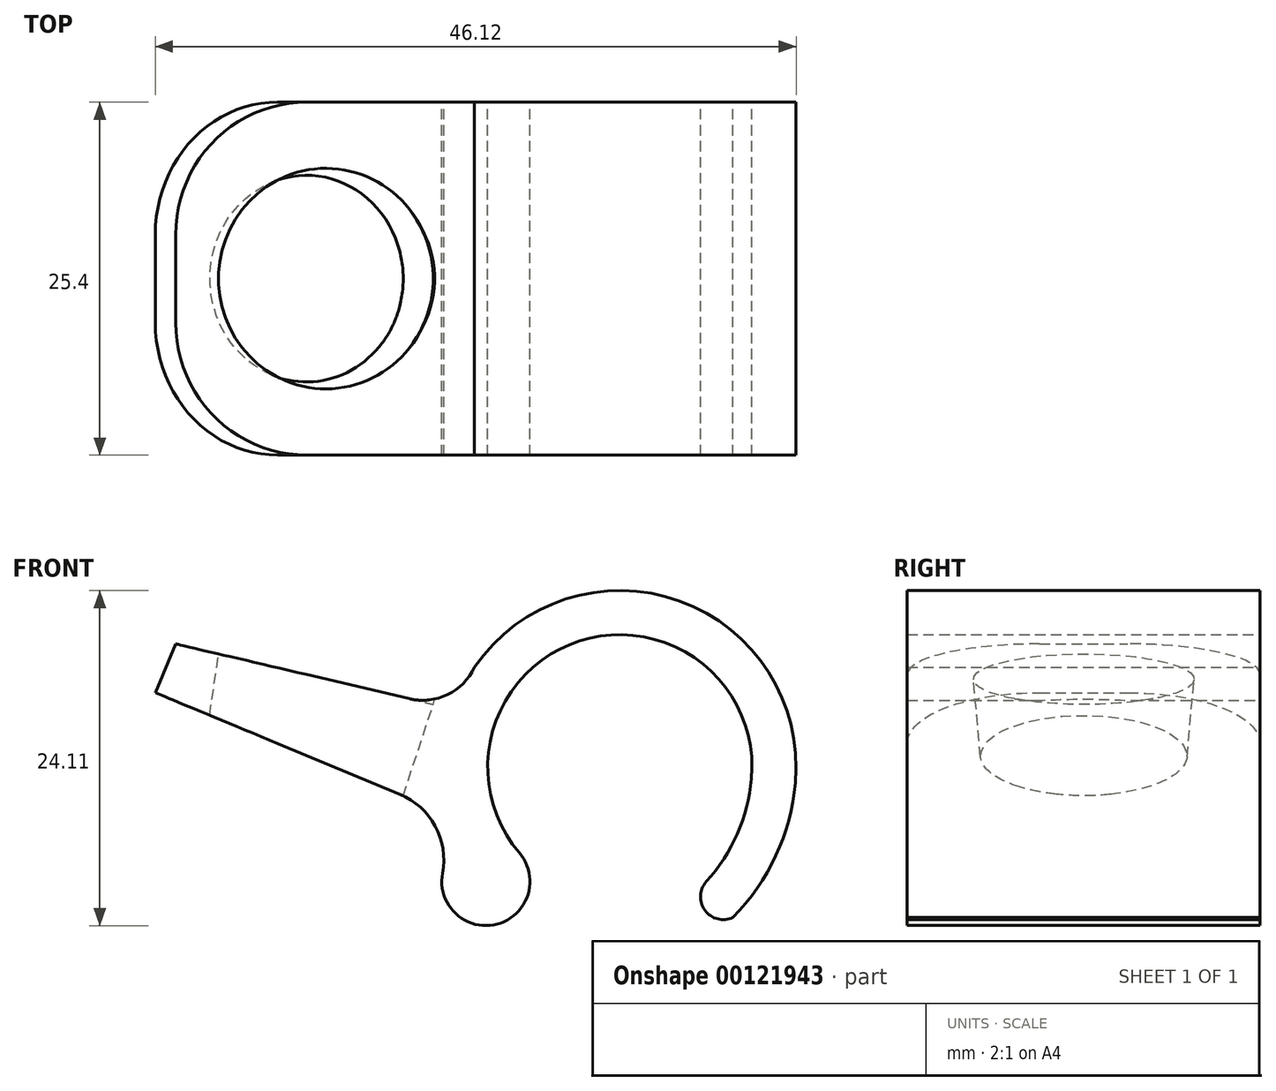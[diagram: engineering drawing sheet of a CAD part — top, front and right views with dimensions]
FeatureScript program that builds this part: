
annotation { "Feature Type Name" : "Feature", "Feature Type Description" : "" }
export const myFeature = defineFeature(function(context is Context, id is Id, definition is map)
    precondition{}
    {
        {
            var Q0;
            Q0=qCreatedBy(makeId("Front.planeOp"),FACE);
            var sketch = newSketch(context, id + "F0", { "sketchPlane" : qUnion([Q0])});
            skLineSegment(sketch, "E0.bottom", {"start": v(0, 0) * mm, "end": v(12.7, 0) * mm, "construction": true});
            skLineSegment(sketch, "E0.top", {"start": v(0, -39.58) * mm, "end": v(12.7, -39.58) * mm, "construction": true});
            skLineSegment(sketch, "E0.left", {"start": v(0, 0) * mm, "end": v(0, -39.58) * mm, "construction": true});
            skLineSegment(sketch, "E0.right", {"start": v(12.7, 0) * mm, "end": v(12.7, -39.58) * mm, "construction": true});
            skArc(sketch, "E1", {"start": v(12.7, -12.7) * mm, "mid": v(14.92, -9.28) * mm, "end": v(15.94, -5.33) * mm});
            skArc(sketch, "E2", {"start": v(-6.3, -12.11) * mm, "mid": v(-2.36, -15.77) * mm, "end": v(-0.76, -10.64) * mm});
            skArc(sketch, "E3", {"start": v(15.94, -5.33) * mm, "mid": v(3.59, 4.6) * mm, "end": v(-0.76, -10.64) * mm});
            skArc(sketch, "E4", {"start": v(-6.3, -12.11) * mm, "mid": v(-6.82, -8.72) * mm, "end": v(-9.37, -6.42) * mm});
            skLineSegment(sketch, "E5", {"start": v(-9.37, -6.42) * mm, "end": v(-26.96, 0.88) * mm});
            skArc(sketch, "E6.0", {"start": v(19.1, -5.62) * mm, "mid": v(10.77, 7.48) * mm, "end": v(-4, 2.72) * mm});
            skArc(sketch, "E6.1", {"start": v(14.62, -15.3) * mm, "mid": v(17.7, -10.84) * mm, "end": v(19.1, -5.62) * mm});
            skArc(sketch, "E7", {"start": v(-8.68, 0.45) * mm, "mid": v(-5.93, 0.75) * mm, "end": v(-4, 2.72) * mm});
            skLineSegment(sketch, "E8", {"start": v(-26.96, 0.88) * mm, "end": v(-25.5, 4.4) * mm});
            skLineSegment(sketch, "E9", {"start": v(-25.5, 4.4) * mm, "end": v(-8.68, 0.45) * mm});
            skArc(sketch, "E10", {"start": v(12.7, -12.7) * mm, "mid": v(12.6, -14.78) * mm, "end": v(14.62, -15.3) * mm});
            skLineSegment(sketch, "E11", {"start": v(12.7, -12.7) * mm, "end": v(14.62, -15.3) * mm, "construction": true});
            skSolve(sketch);
        }
        {
            var Q0;
            Q0 = qSketchRegion(id + "F0", true);
            extrude(context, id + "F1", {"entities" : qUnion([Q0]), "depth" : 25.4 * mm});
        }
        {
            var Q0;
            Q0=makeQuery(id+"F1.opExtrude","SWEPT_FACE",FACE,{"disambiguationData":[OSD([sQuery(id+"F0.wireOp",EDGE,"E9")])]});
            var sketch = newSketch(context, id + "F2", { "sketchPlane" : qUnion([Q0])});
            skCircle(sketch, "E12", {"center": v(-14.72, -12.7) * mm, "radius": 7.94 * mm});
            skLineSegment(sketch, "E13", {"start": v(-25.83, -12.7) * mm, "end": v(-14.72, -12.7) * mm, "construction": true});
            skPoint(sketch, "E14", {"position": v(-22.66, -12.7) * mm});
            skSolve(sketch);
        }
        {
            var Q0;
            Q0 = qSketchRegion(id + "F2", true);
            extrude(context, id + "F3", {"entities" : qUnion([Q0]), "operationType" : NewBodyOperationType.REMOVE, "oppositeDirection" : true, "depth" : 25.4 * mm, "hasDraft" : true, "draftAngle" : 5 * degree, "draftPullDirection" : true, "hasSecondDirection" : true, "secondDirectionOppositeDirection" : false, "secondDirectionDepth" : 25.4 * mm});
        }
        {
            var Q0;
            Q0=makeQuery(id+"F1.opExtrude","CAP_EDGE",EDGE,{"disambiguationData":[OSD([sQuery(id+"F0.wireOp",EDGE,"E8")])],"isStart":true});
            var Q1;
            Q1=makeQuery(id+"F1.opExtrude","CAP_EDGE",EDGE,{"disambiguationData":[OSD([sQuery(id+"F0.wireOp",EDGE,"E8")])],"isStart":false});
            fillet(context, id + "F4", {"entities" : qUnion([Q0, Q1]), "radius" : 9.52 * mm, "tangentPropagation" : true, "allowEdgeOverflow" : false});
        }
    });
